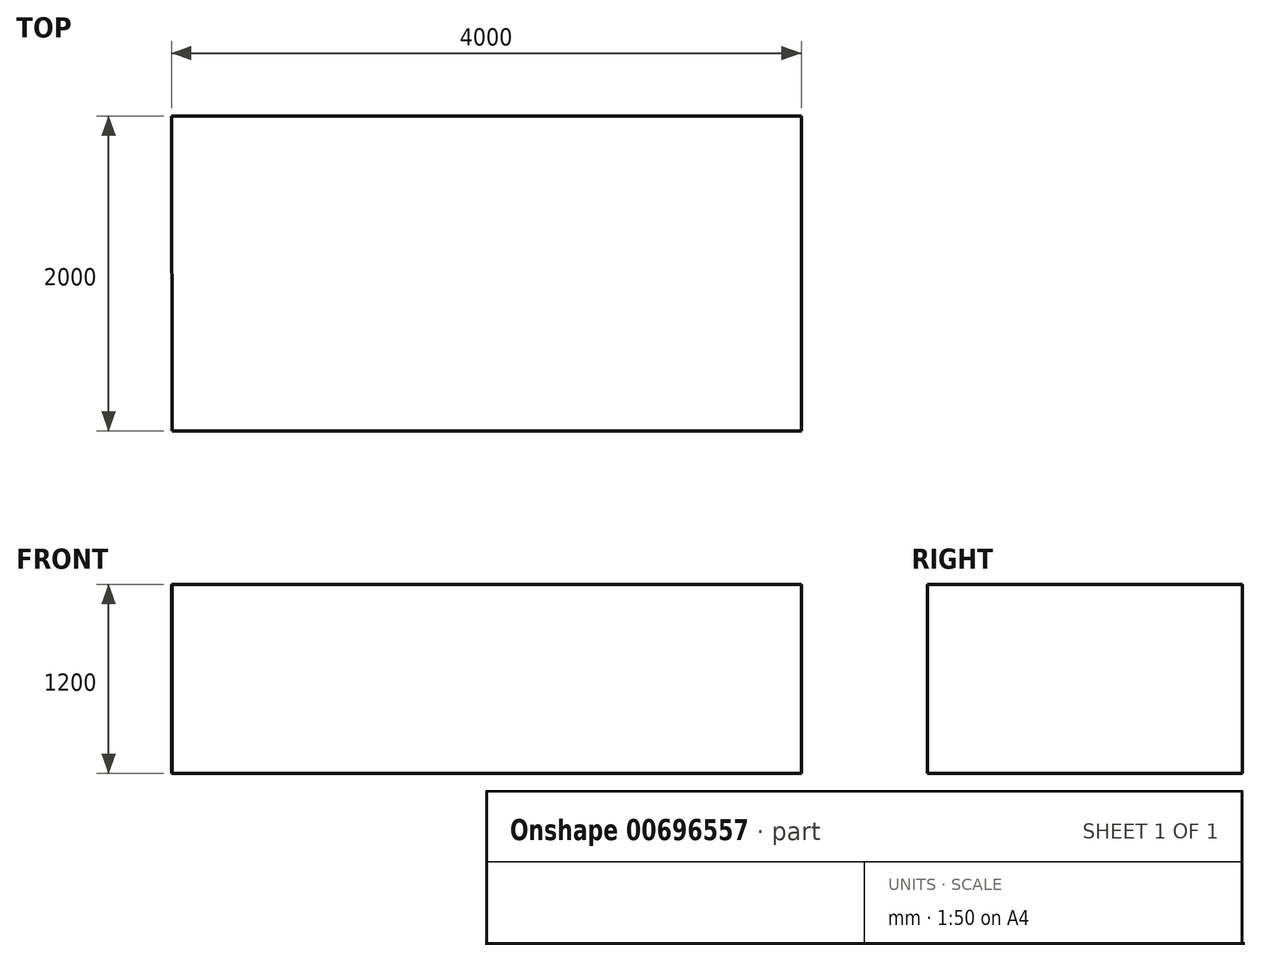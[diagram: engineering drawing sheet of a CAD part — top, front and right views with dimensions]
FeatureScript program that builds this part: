
annotation { "Feature Type Name" : "Feature", "Feature Type Description" : "" }
export const myFeature = defineFeature(function(context is Context, id is Id, definition is map)
    precondition{}
    {
        {
            var Q0;
            Q0=qCreatedBy(makeId("Top.planeOp"),FACE);
            var sketch = newSketch(context, id + "F0", { "sketchPlane" : qUnion([Q0])});
            skLineSegment(sketch, "E0", {"start": v(-1995.72, 1195.71) * mm, "end": v(2004.28, 1195.71) * mm});
            skLineSegment(sketch, "E1", {"start": v(2004.28, 1195.71) * mm, "end": v(2004.28, -804.29) * mm});
            skLineSegment(sketch, "E2", {"start": v(2004.28, -804.29) * mm, "end": v(-1990.43, -804.29) * mm});
            skLineSegment(sketch, "E3", {"start": v(-1990.43, -804.29) * mm, "end": v(-1995.72, 1195.71) * mm});
            skSolve(sketch);
        }
        {
            var Q0;
            Q0=sQuery(id+"F0.wireOp",EDGE,"E0");
            var Q1;
            Q1=sQuery(id+"F0.wireOp",EDGE,"E3");
            var Q2;
            Q2=sQuery(id+"F0.wireOp",EDGE,"E1");
            var Q3;
            Q3=sQuery(id+"F0.wireOp",EDGE,"E2");
            extrude(context, id + "F1", {"bodyType" : ToolBodyType.SURFACE, "surfaceEntities" : qUnion([Q0, Q1, Q2, Q3]), "depth" : 1200 * mm, "offsetDistance" : 25 * mm});
        }
    });
